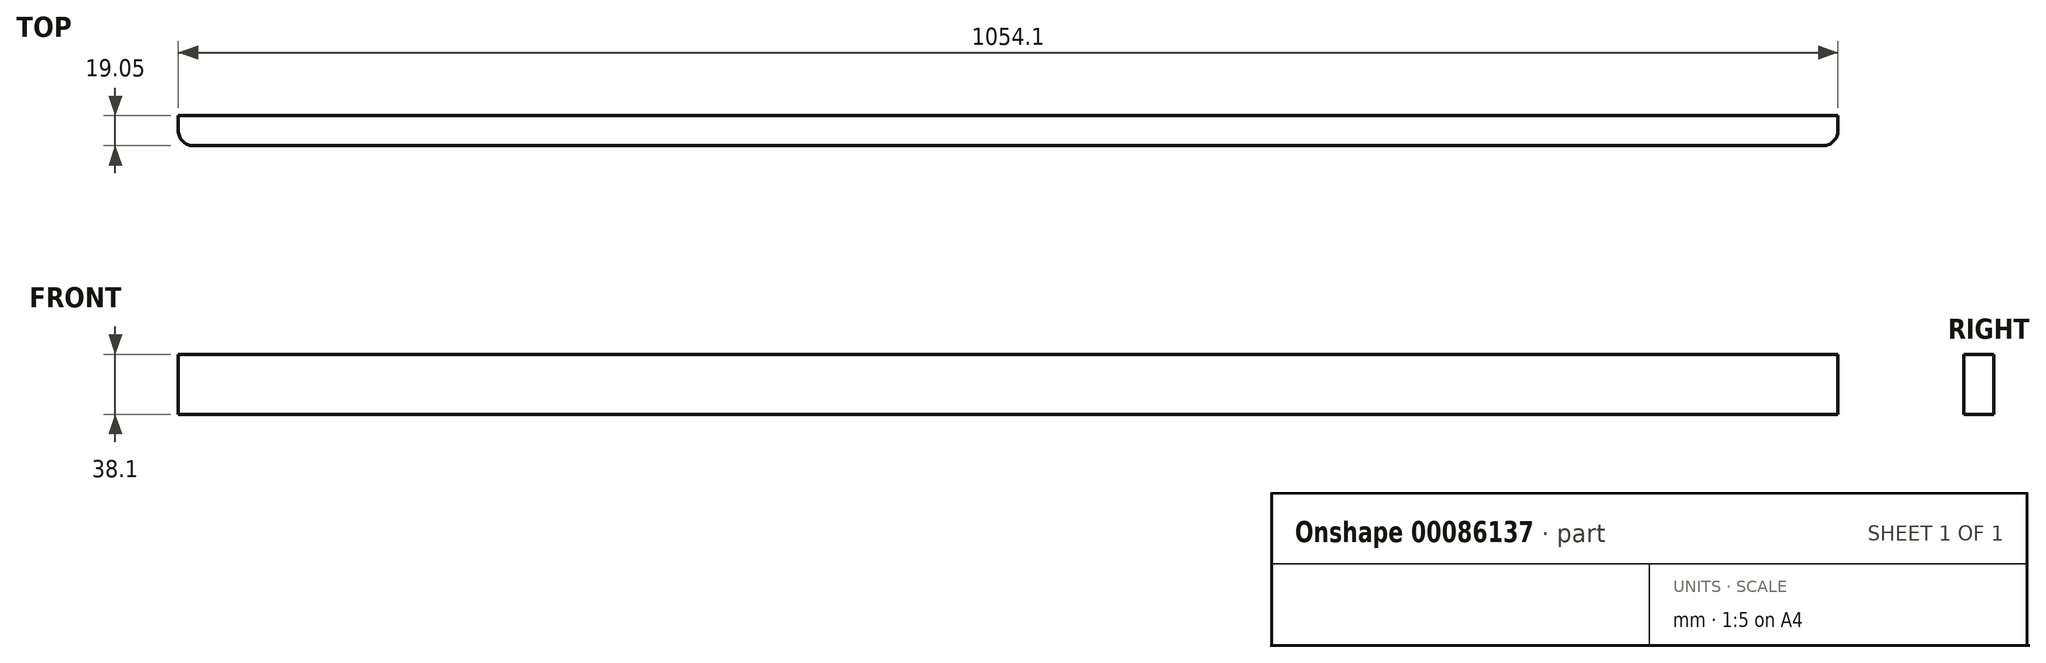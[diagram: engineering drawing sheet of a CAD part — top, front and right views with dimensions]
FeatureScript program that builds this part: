
annotation { "Feature Type Name" : "Feature", "Feature Type Description" : "" }
export const myFeature = defineFeature(function(context is Context, id is Id, definition is map)
    precondition{}
    {
        {
            var Q0;
            Q0=qCreatedBy(makeId("Front.planeOp"),FACE);
            var sketch = newSketch(context, id + "F0", { "sketchPlane" : qUnion([Q0])});
            skLineSegment(sketch, "E0.bottom", {"start": v(539.64, -19.05) * mm, "end": v(-514.46, -19.05) * mm});
            skLineSegment(sketch, "E0.top", {"start": v(539.64, 19.05) * mm, "end": v(-514.46, 19.05) * mm});
            skLineSegment(sketch, "E0.left", {"start": v(539.64, -19.05) * mm, "end": v(539.64, 19.05) * mm});
            skLineSegment(sketch, "E0.right", {"start": v(-514.46, -19.05) * mm, "end": v(-514.46, 19.05) * mm});
            skPoint(sketch, "E0.middle", {"position": v(12.59, 0) * mm});
            skSolve(sketch);
        }
        {
            var Q0;
            Q0 = qSketchRegion(id + "F0", true);
            extrude(context, id + "F1", {"entities" : qUnion([Q0]), "depth" : 19.05 * mm});
        }
        {
            var Q0;
            Q0=makeQuery(id+"F1.opExtrude","CAP_EDGE",EDGE,{"disambiguationData":[OSD([sQuery(id+"F0.wireOp",EDGE,"E0.left")])],"isStart":false});
            var Q1;
            Q1=makeQuery(id+"F1.opExtrude","CAP_EDGE",EDGE,{"disambiguationData":[OSD([sQuery(id+"F0.wireOp",EDGE,"E0.right")])],"isStart":false});
            fillet(context, id + "F2", {"entities" : qUnion([Q0, Q1]), "radius" : 9.52 * mm, "tangentPropagation" : true, "allowEdgeOverflow" : false});
        }
    });
